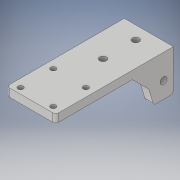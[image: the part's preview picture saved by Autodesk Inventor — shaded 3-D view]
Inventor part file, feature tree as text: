
AUTODESK INVENTOR PART (.ipt)
format: ipt  version: 2018 (Build 220112000, 112)  size: 185,856 bytes
history: native  units: in
note: dims shown in document units (in); Inventor stores cm internally (conversion verified against a paired STEP export)
features: extrude x6, sketch x5, mirror x1, fillet x1, chamfer x1, plane x1
ambient origin geometry x8: Origin, YZ Plane, XZ Plane, XY Plane, X Axis, Y Axis, Z Axis, Center Point
bodies: Solid1 (feature_tree)
feature tree (15):
  extrude  "Extrusion1"  Depth=2.8346in
  extrude  "Extrusion2"  Depth=0.1969in
  extrude  "Extrusion3"  Depth=0.7874in
  extrude  "Extrusion4"  Depth=0.1969in TaperAngle=0.0deg
  mirror  "Mirror2"
  extrude  "Extrusion8"  Depth=0.7874in
  fillet  "Fillet2"  Radius=0.1969in
  extrude  "Extrusion9"  Depth=0.1969in TaperAngle=0.0deg
  chamfer  "Chamfer1"  Distance=0.9843in
  sketch  "Sketch1"  dims[d0=1.1811in d1=2.8346in]
  sketch  "Sketch2"  dims[d2=0.1969in d3=0.0in d4=0.126in]
  sketch  "Sketch3"  dims[d5=0.7874in d6=0.7874in]
  plane  "Work Plane1"
  sketch  "Sketch8"  dims[d7=0.1378in d8=0.1969in d9=0.0in]
  sketch  "Sketch9"  dims[d12=0.1654in d14=0.7874in d15=0.1969in d16=0.0in d20=0.1969in d21=0.0in d33=0.9843in d34=45.0deg d35=0.7874in d38=0.4724in d39=0.1654in d40=0.3937in d41=0.3937in d42=0.0in d43=0.0787in d44=1.2992in d45=0.1181in d46=0.5512in d47=0.1181in d48=0.0in d49=0.0787in d50=0.0787in d51=45.0deg d52=0.315in]
